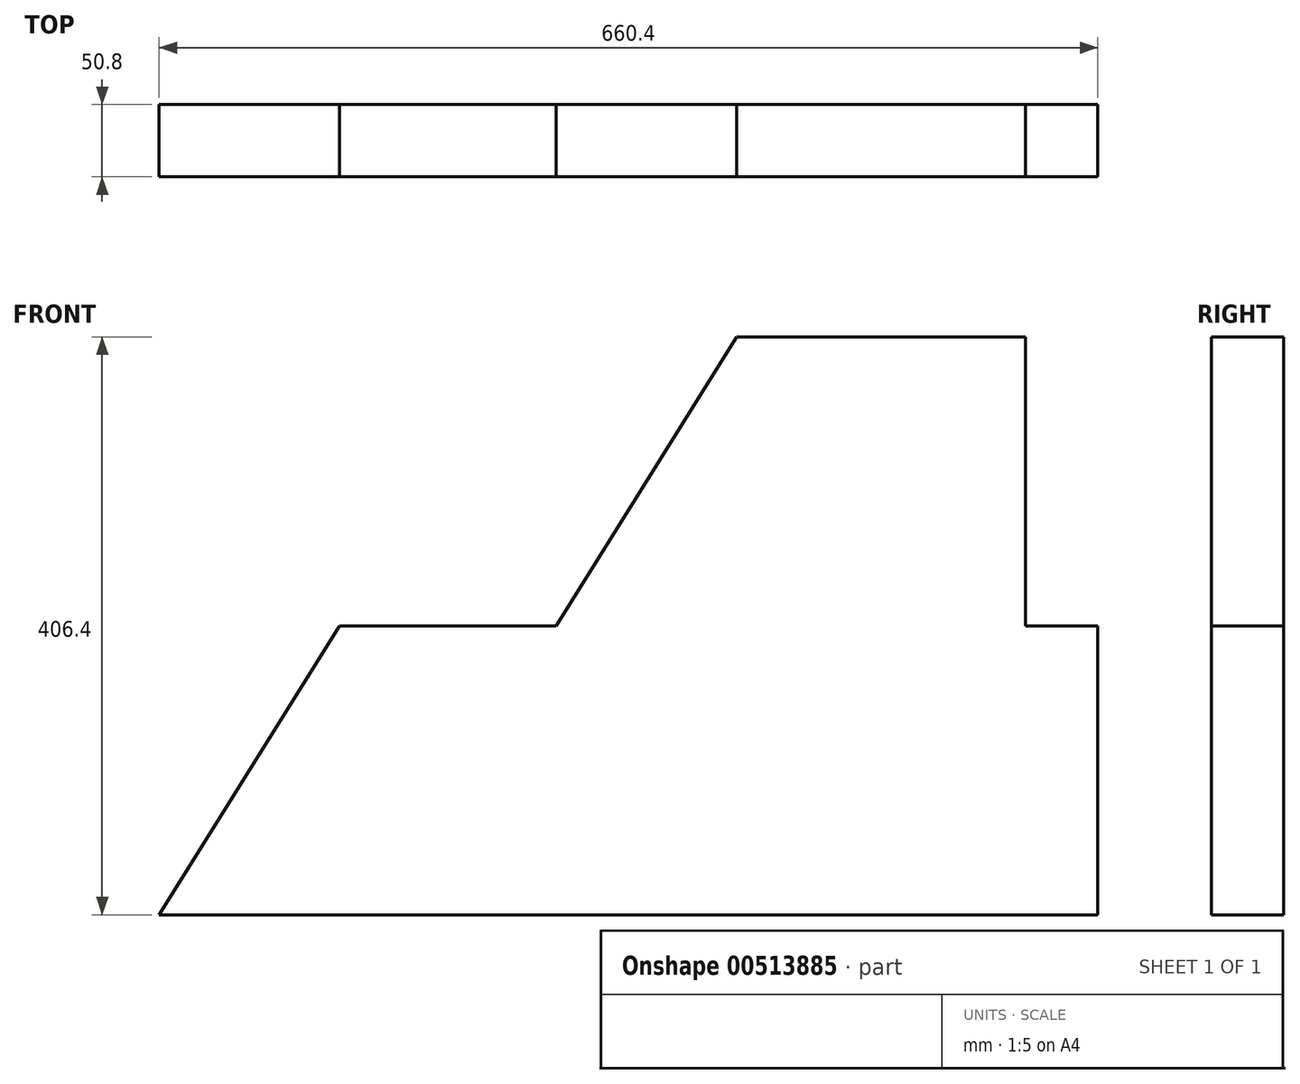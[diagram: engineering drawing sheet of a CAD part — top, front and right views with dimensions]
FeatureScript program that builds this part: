
annotation { "Feature Type Name" : "Feature", "Feature Type Description" : "" }
export const myFeature = defineFeature(function(context is Context, id is Id, definition is map)
    precondition{}
    {
        {
            var Q0;
            Q0=qCreatedBy(makeId("Front.planeOp"),FACE);
            var sketch = newSketch(context, id + "F0", { "sketchPlane" : qUnion([Q0])});
            skLineSegment(sketch, "E0", {"start": v(0, 0) * mm, "end": v(660.4, 0) * mm});
            skLineSegment(sketch, "E1", {"start": v(660.4, 0) * mm, "end": v(660.4, 203.2) * mm});
            skLineSegment(sketch, "E2", {"start": v(660.4, 203.2) * mm, "end": v(609.6, 203.2) * mm});
            skLineSegment(sketch, "E3", {"start": v(609.6, 203.2) * mm, "end": v(609.6, 406.4) * mm});
            skLineSegment(sketch, "E4", {"start": v(609.6, 406.4) * mm, "end": v(406.4, 406.4) * mm});
            skLineSegment(sketch, "E5", {"start": v(406.4, 406.4) * mm, "end": v(279.4, 203.2) * mm});
            skLineSegment(sketch, "E6", {"start": v(279.4, 203.2) * mm, "end": v(127, 203.2) * mm});
            skLineSegment(sketch, "E7", {"start": v(127, 203.2) * mm, "end": v(0, 0) * mm});
            skSolve(sketch);
        }
        {
            var Q0;
            Q0 = qSketchRegion(id + "F0", true);
            extrude(context, id + "F1", {"entities" : qUnion([Q0]), "depth" : 50.8 * mm, "offsetDistance" : 25.4 * mm});
        }
    });
